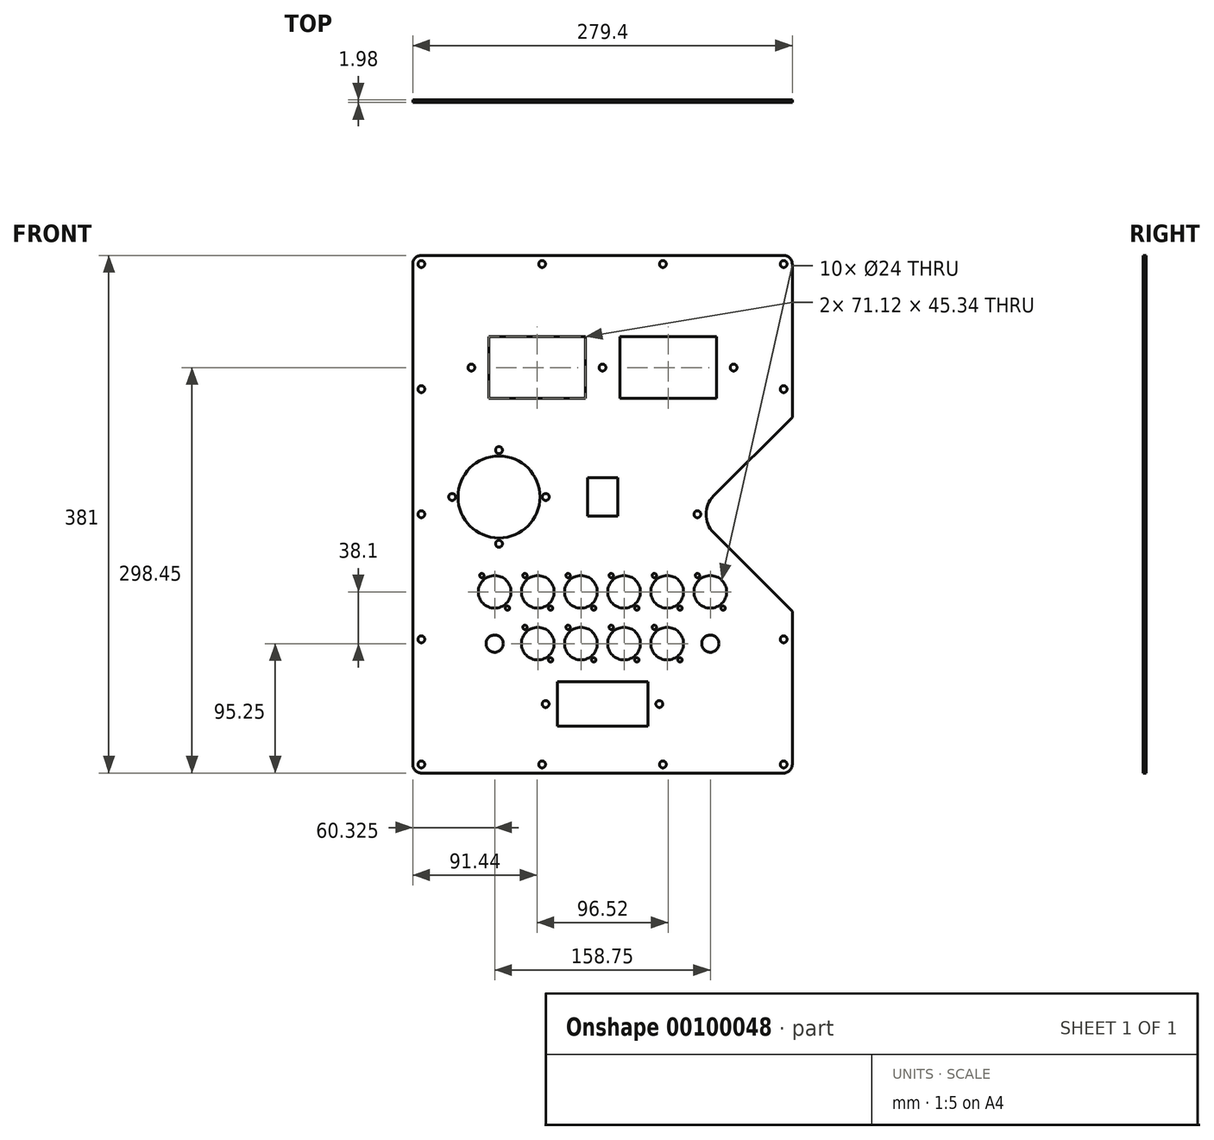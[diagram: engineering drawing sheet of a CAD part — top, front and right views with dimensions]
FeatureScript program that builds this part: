
annotation { "Feature Type Name" : "Feature", "Feature Type Description" : "" }
export const myFeature = defineFeature(function(context is Context, id is Id, definition is map)
    precondition{}
    {
        {
            var Q0;
            Q0=qCreatedBy(makeId("Front.planeOp"),FACE);
            var sketch = newSketch(context, id + "F0", { "sketchPlane" : qUnion([Q0])});
            skLineSegment(sketch, "E0.bottom", {"start": v(-139.7, 190.5) * mm, "end": v(139.7, 190.5) * mm});
            skLineSegment(sketch, "E0.top", {"start": v(-139.7, -190.5) * mm, "end": v(139.7, -190.5) * mm});
            skLineSegment(sketch, "E0.left", {"start": v(-139.7, 190.5) * mm, "end": v(-139.7, -190.5) * mm});
            skLineSegment(sketch, "E0.right", {"start": v(139.7, 190.5) * mm, "end": v(139.7, -190.5) * mm});
            skLineSegment(sketch, "E1", {"start": v(-139.7, 190.5) * mm, "end": v(139.7, -190.5) * mm, "construction": true});
            skLineSegment(sketch, "E2", {"start": v(139.7, 190.5) * mm, "end": v(-139.7, -190.5) * mm, "construction": true});
            skLineSegment(sketch, "E3", {"start": v(0, 190.5) * mm, "end": v(0, -190.5) * mm, "construction": true});
            skSolve(sketch);
        }
        {
            var Q0;
            Q0 = qSketchRegion(id + "F0", true);
            extrude(context, id + "F1", {"entities" : qUnion([Q0]), "depth" : 1.98 * mm});
        }
        {
            var Q0;
            Q0=makeQuery(id+"F1.opExtrude","CAP_FACE",FACE,{"disambiguationData":[OSD([sQuery(id+"F0.wireOp",EDGE,"E0.bottom"),sQuery(id+"F0.wireOp",EDGE,"E0.top"),sQuery(id+"F0.wireOp",EDGE,"E0.left"),sQuery(id+"F0.wireOp",EDGE,"E0.right")])],"isStart":false});
            var sketch = newSketch(context, id + "F2", { "sketchPlane" : qUnion([Q0])});
            skLineSegment(sketch, "E4.bottom", {"start": v(127, 177.8) * mm, "end": v(-127, 177.8) * mm});
            skLineSegment(sketch, "E4.top", {"start": v(127, -177.8) * mm, "end": v(-127, -177.8) * mm});
            skLineSegment(sketch, "E4.left", {"start": v(127, 177.8) * mm, "end": v(127, 76.65) * mm});
            skLineSegment(sketch, "E4.right", {"start": v(-127, 177.8) * mm, "end": v(-127, -177.8) * mm});
            skPoint(sketch, "E4.middle", {"position": v(0, 0) * mm});
            skArc(sketch, "E5", {"start": v(72.8, 22.45) * mm, "mid": v(63.5, 0) * mm, "end": v(72.8, -22.45) * mm});
            skLineSegment(sketch, "E6", {"start": v(72.8, 22.45) * mm, "end": v(127, 76.65) * mm});
            skLineSegment(sketch, "E7", {"start": v(72.8, -22.45) * mm, "end": v(127, -76.65) * mm});
            skLineSegment(sketch, "E8.trimOffspring", {"start": v(127, -76.65) * mm, "end": v(127, -177.8) * mm});
            skSolve(sketch);
        }
        {
            var Q0;
            Q0=makeQuery(id+"F1.opExtrude","CAP_FACE",FACE,{"disambiguationData":[OSD([sQuery(id+"F0.wireOp",EDGE,"E0.bottom"),sQuery(id+"F0.wireOp",EDGE,"E0.top"),sQuery(id+"F0.wireOp",EDGE,"E0.left"),sQuery(id+"F0.wireOp",EDGE,"E0.right")])],"isStart":false});
            var sketch = newSketch(context, id + "F3", { "sketchPlane" : qUnion([Q0])});
            skCircle(sketch, "E9", {"center": v(-76.2, 12.7) * mm, "radius": 30.16 * mm});
            skCircle(sketch, "E10", {"center": v(-76.2, 47.16) * mm, "radius": 2.54 * mm});
            skCircle(sketch, "E11", {"center": v(-41.74, 12.7) * mm, "radius": 2.54 * mm});
            skCircle(sketch, "E12", {"center": v(-76.2, -21.76) * mm, "radius": 2.54 * mm});
            skCircle(sketch, "E13", {"center": v(-110.66, 12.7) * mm, "radius": 2.54 * mm});
            skCircle(sketch, "E14", {"center": v(-76.2, 12.7) * mm, "radius": 34.46 * mm, "construction": true});
            skSolve(sketch);
        }
        {
            var Q0;
            Q0=makeQuery(id+"F1.opExtrude","CAP_FACE",FACE,{"disambiguationData":[OSD([sQuery(id+"F0.wireOp",EDGE,"E0.bottom"),sQuery(id+"F0.wireOp",EDGE,"E0.top"),sQuery(id+"F0.wireOp",EDGE,"E0.left"),sQuery(id+"F0.wireOp",EDGE,"E0.right")])],"isStart":false});
            var sketch = newSketch(context, id + "F4", { "sketchPlane" : qUnion([Q0])});
            skLineSegment(sketch, "E15.bottom", {"start": v(-11.11, 26.76) * mm, "end": v(11.11, 26.76) * mm});
            skLineSegment(sketch, "E15.top", {"start": v(-11.11, -1.36) * mm, "end": v(11.11, -1.36) * mm});
            skLineSegment(sketch, "E15.left", {"start": v(-11.11, 26.76) * mm, "end": v(-11.11, -1.36) * mm});
            skLineSegment(sketch, "E15.right", {"start": v(11.11, 26.76) * mm, "end": v(11.11, -1.36) * mm});
            skLineSegment(sketch, "E16", {"start": v(0, -1.36) * mm, "end": v(0, 0) * mm, "construction": true});
            skCircle(sketch, "E17.0", {"center": v(-76.2, 12.7) * mm, "radius": 34.46 * mm, "construction": true});
            skLineSegment(sketch, "E18", {"start": v(-76.2, 12.7) * mm, "end": v(-11.11, 12.7) * mm, "construction": true});
            skSolve(sketch);
        }
        {
            var Q0;
            Q0=makeQuery(id+"F1.opExtrude","CAP_FACE",FACE,{"disambiguationData":[OSD([sQuery(id+"F0.wireOp",EDGE,"E0.bottom"),sQuery(id+"F0.wireOp",EDGE,"E0.top"),sQuery(id+"F0.wireOp",EDGE,"E0.left"),sQuery(id+"F0.wireOp",EDGE,"E0.right")])],"isStart":false});
            var sketch = newSketch(context, id + "F5", { "sketchPlane" : qUnion([Q0])});
            skLineSegment(sketch, "E19.bottom", {"start": v(-83.82, 85.28) * mm, "end": v(-12.7, 85.28) * mm});
            skLineSegment(sketch, "E19.top", {"start": v(-83.82, 130.62) * mm, "end": v(-12.7, 130.62) * mm});
            skLineSegment(sketch, "E19.left", {"start": v(-83.82, 85.28) * mm, "end": v(-83.82, 130.62) * mm});
            skLineSegment(sketch, "E19.right", {"start": v(-12.7, 85.28) * mm, "end": v(-12.7, 130.62) * mm});
            skLineSegment(sketch, "E20.bottom", {"start": v(12.7, 85.28) * mm, "end": v(83.82, 85.28) * mm});
            skLineSegment(sketch, "E20.top", {"start": v(12.7, 130.62) * mm, "end": v(83.82, 130.62) * mm});
            skLineSegment(sketch, "E20.left", {"start": v(12.7, 85.28) * mm, "end": v(12.7, 130.62) * mm});
            skLineSegment(sketch, "E20.right", {"start": v(83.82, 85.28) * mm, "end": v(83.82, 130.62) * mm});
            skLineSegment(sketch, "E21", {"start": v(-83.82, 107.95) * mm, "end": v(-96.52, 107.95) * mm, "construction": true});
            skLineSegment(sketch, "E22", {"start": v(83.82, 107.95) * mm, "end": v(96.52, 107.95) * mm, "construction": true});
            skCircle(sketch, "E23", {"center": v(-96.52, 107.95) * mm, "radius": 2.54 * mm});
            skCircle(sketch, "E24", {"center": v(96.52, 107.95) * mm, "radius": 2.54 * mm});
            skLineSegment(sketch, "E25", {"start": v(-12.7, 107.95) * mm, "end": v(0, 107.95) * mm, "construction": true});
            skPoint(sketch, "E25.endSnap0", {"position": v(-12.7, 107.95) * mm});
            skLineSegment(sketch, "E26", {"start": v(12.7, 107.95) * mm, "end": v(0, 107.95) * mm, "construction": true});
            skCircle(sketch, "E27", {"center": v(0, 107.95) * mm, "radius": 2.54 * mm});
            skLineSegment(sketch, "E28", {"start": v(0, 107.95) * mm, "end": v(0, 0) * mm, "construction": true});
            skSolve(sketch);
        }
        {
            var Q0;
            Q0=makeQuery(id+"F1.opExtrude","CAP_FACE",FACE,{"disambiguationData":[OSD([sQuery(id+"F0.wireOp",EDGE,"E0.bottom"),sQuery(id+"F0.wireOp",EDGE,"E0.top"),sQuery(id+"F0.wireOp",EDGE,"E0.left"),sQuery(id+"F0.wireOp",EDGE,"E0.right"),sQuery(id+"F0.wireOp",EDGE,"h9IRMIpb-LSlu-fdTu-ycnf-mhpyygmtLJdv"),sQuery(id+"F0.wireOp",EDGE,"yYoEWnjZ-7jQh-CGfM-oPbc-j7pyWlvO7h1l"),sQuery(id+"F0.wireOp",EDGE,"NovJv7q1-vMpo-y6lM-6HwO-RKcohdMXKd2X"),sQuery(id+"F0.wireOp",EDGE,"Jd78Q13S-E8d5-oNmg-n0Bc-iBzX8L0d9LYk"),sQuery(id+"F0.wireOp",EDGE,"d569440b-4b0a-41ca-b9de-1d57797d9db2.0.1.0"),sQuery(id+"F0.wireOp",EDGE,"d569440b-4b0a-41ca-b9de-1d57797d9db2.0.1.1"),sQuery(id+"F0.wireOp",EDGE,"d569440b-4b0a-41ca-b9de-1d57797d9db2.0.1.2"),sQuery(id+"F0.wireOp",EDGE,"d569440b-4b0a-41ca-b9de-1d57797d9db2.0.1.3"),sQuery(id+"F0.wireOp",EDGE,"590198d3-f6c1-4934-8355-473c2aef56420.MirrorCS"),sQuery(id+"F0.wireOp",EDGE,"fb5975e0-c9aa-4f66-85a4-b5ec14ec1ced0.MirrorCS"),sQuery(id+"F0.wireOp",EDGE,"d673b164-0bbc-45ec-aa36-e85b659530970.MirrorCS"),sQuery(id+"F0.wireOp",EDGE,"a6f88071-2a8c-472b-9538-4447b179ac7b0.MirrorCS"),sQuery(id+"F0.wireOp",EDGE,"384c53e7-d2bd-4482-b8c2-024507e4105a0.MirrorCS"),sQuery(id+"F0.wireOp",EDGE,"c5e2c4c2-971b-4f43-83ae-2127a011e6c90.MirrorCS"),sQuery(id+"F0.wireOp",EDGE,"ec55bebb-8ae0-4cb5-937d-f917f98a93640.MirrorCS"),sQuery(id+"F0.wireOp",EDGE,"7c94f603-0cc5-4a8e-8c4c-9db3a374b4de0.MirrorCS")])],"isStart":false});
            var sketch = newSketch(context, id + "F6", { "sketchPlane" : qUnion([Q0])});
            skCircle(sketch, "E29", {"center": v(-79.37, -57.15) * mm, "radius": 12 * mm});
            skCircle(sketch, "E30", {"center": v(-88.84, -45.15) * mm, "radius": 1.59 * mm});
            skCircle(sketch, "E31", {"center": v(-69.91, -69.15) * mm, "radius": 1.59 * mm});
            skLineSegment(sketch, "E32", {"start": v(-79.37, -57.15) * mm, "end": v(-88.84, -45.15) * mm, "construction": true});
            skLineSegment(sketch, "E33", {"start": v(-79.37, -57.15) * mm, "end": v(-69.91, -69.15) * mm, "construction": true});
            skCircle(sketch, "E34.1.0.0", {"center": v(-47.62, -57.15) * mm, "radius": 12 * mm});
            skCircle(sketch, "E34.1.0.1", {"center": v(-57.09, -45.15) * mm, "radius": 1.59 * mm});
            skCircle(sketch, "E34.1.0.2", {"center": v(-38.16, -69.15) * mm, "radius": 1.59 * mm});
            skLineSegment(sketch, "E34.1.0.3", {"start": v(-47.62, -57.15) * mm, "end": v(-38.16, -69.15) * mm, "construction": true});
            skLineSegment(sketch, "E34.1.0.4", {"start": v(-47.62, -57.15) * mm, "end": v(-57.09, -45.15) * mm, "construction": true});
            skCircle(sketch, "E34.2.0.0", {"center": v(-15.87, -57.15) * mm, "radius": 12 * mm});
            skCircle(sketch, "E34.2.0.1", {"center": v(-25.34, -45.15) * mm, "radius": 1.59 * mm});
            skCircle(sketch, "E34.2.0.2", {"center": v(-6.41, -69.15) * mm, "radius": 1.59 * mm});
            skLineSegment(sketch, "E34.2.0.3", {"start": v(-15.87, -57.15) * mm, "end": v(-6.41, -69.15) * mm, "construction": true});
            skLineSegment(sketch, "E34.2.0.4", {"start": v(-15.87, -57.15) * mm, "end": v(-25.34, -45.15) * mm, "construction": true});
            skCircle(sketch, "E34.3.0.0", {"center": v(15.88, -57.15) * mm, "radius": 12 * mm});
            skCircle(sketch, "E34.3.0.1", {"center": v(6.41, -45.15) * mm, "radius": 1.59 * mm});
            skCircle(sketch, "E34.3.0.2", {"center": v(25.34, -69.15) * mm, "radius": 1.59 * mm});
            skLineSegment(sketch, "E34.3.0.3", {"start": v(15.88, -57.15) * mm, "end": v(25.34, -69.15) * mm, "construction": true});
            skLineSegment(sketch, "E34.3.0.4", {"start": v(15.88, -57.15) * mm, "end": v(6.41, -45.15) * mm, "construction": true});
            skCircle(sketch, "E34.4.0.0", {"center": v(47.62, -57.15) * mm, "radius": 12 * mm});
            skCircle(sketch, "E34.4.0.1", {"center": v(38.16, -45.15) * mm, "radius": 1.59 * mm});
            skCircle(sketch, "E34.4.0.2", {"center": v(57.09, -69.15) * mm, "radius": 1.59 * mm});
            skLineSegment(sketch, "E34.4.0.3", {"start": v(47.63, -57.15) * mm, "end": v(57.09, -69.15) * mm, "construction": true});
            skLineSegment(sketch, "E34.4.0.4", {"start": v(47.63, -57.15) * mm, "end": v(38.16, -45.15) * mm, "construction": true});
            skCircle(sketch, "E34.5.0.0", {"center": v(79.37, -57.15) * mm, "radius": 12 * mm});
            skCircle(sketch, "E34.5.0.1", {"center": v(69.91, -45.15) * mm, "radius": 1.59 * mm});
            skCircle(sketch, "E34.5.0.2", {"center": v(88.84, -69.15) * mm, "radius": 1.59 * mm});
            skLineSegment(sketch, "E34.5.0.3", {"start": v(79.38, -57.15) * mm, "end": v(88.84, -69.15) * mm, "construction": true});
            skLineSegment(sketch, "E34.5.0.4", {"start": v(79.38, -57.15) * mm, "end": v(69.91, -45.15) * mm, "construction": true});
            skLineSegment(sketch, "E34.direction1", {"start": v(-79.37, -57.15) * mm, "end": v(-47.62, -57.15) * mm, "construction": true});
            skLineSegment(sketch, "E35", {"start": v(-15.87, -57.15) * mm, "end": v(15.88, -57.15) * mm, "construction": true});
            skLineSegment(sketch, "E36", {"start": v(0, 0) * mm, "end": v(0, -57.15) * mm, "construction": true});
            skSolve(sketch);
        }
        {
            var Q0;
            Q0=makeQuery(id+"F1.opExtrude","CAP_FACE",FACE,{"disambiguationData":[OSD([sQuery(id+"F0.wireOp",EDGE,"E0.bottom"),sQuery(id+"F0.wireOp",EDGE,"E0.top"),sQuery(id+"F0.wireOp",EDGE,"E0.left"),sQuery(id+"F0.wireOp",EDGE,"E0.right")])],"isStart":false});
            var sketch = newSketch(context, id + "F7", { "sketchPlane" : qUnion([Q0])});
            skCircle(sketch, "E37", {"center": v(-47.62, -95.25) * mm, "radius": 12 * mm});
            skCircle(sketch, "E38", {"center": v(-57.09, -83.25) * mm, "radius": 1.59 * mm});
            skCircle(sketch, "E39", {"center": v(-38.16, -107.25) * mm, "radius": 1.59 * mm});
            skLineSegment(sketch, "E40", {"start": v(-57.09, -83.25) * mm, "end": v(-47.62, -95.25) * mm, "construction": true});
            skLineSegment(sketch, "E41", {"start": v(-38.16, -107.25) * mm, "end": v(-47.62, -95.25) * mm, "construction": true});
            skCircle(sketch, "E42.1.0.0", {"center": v(-15.87, -95.25) * mm, "radius": 12 * mm});
            skLineSegment(sketch, "E42.1.0.1", {"start": v(-6.41, -107.25) * mm, "end": v(-15.87, -95.25) * mm, "construction": true});
            skLineSegment(sketch, "E42.1.0.2", {"start": v(-25.34, -83.25) * mm, "end": v(-15.87, -95.25) * mm, "construction": true});
            skCircle(sketch, "E42.1.0.3", {"center": v(-25.34, -83.25) * mm, "radius": 1.59 * mm});
            skCircle(sketch, "E42.1.0.4", {"center": v(-6.41, -107.25) * mm, "radius": 1.59 * mm});
            skCircle(sketch, "E42.2.0.0", {"center": v(15.88, -95.25) * mm, "radius": 12 * mm});
            skLineSegment(sketch, "E42.2.0.1", {"start": v(25.34, -107.25) * mm, "end": v(15.88, -95.25) * mm, "construction": true});
            skLineSegment(sketch, "E42.2.0.2", {"start": v(6.41, -83.25) * mm, "end": v(15.88, -95.25) * mm, "construction": true});
            skCircle(sketch, "E42.2.0.3", {"center": v(6.41, -83.25) * mm, "radius": 1.59 * mm});
            skCircle(sketch, "E42.2.0.4", {"center": v(25.34, -107.25) * mm, "radius": 1.59 * mm});
            skCircle(sketch, "E42.3.0.0", {"center": v(47.63, -95.25) * mm, "radius": 12 * mm});
            skLineSegment(sketch, "E42.3.0.1", {"start": v(57.09, -107.25) * mm, "end": v(47.63, -95.25) * mm, "construction": true});
            skLineSegment(sketch, "E42.3.0.2", {"start": v(38.16, -83.25) * mm, "end": v(47.63, -95.25) * mm, "construction": true});
            skCircle(sketch, "E42.3.0.3", {"center": v(38.16, -83.25) * mm, "radius": 1.59 * mm});
            skCircle(sketch, "E42.3.0.4", {"center": v(57.09, -107.25) * mm, "radius": 1.59 * mm});
            skLineSegment(sketch, "E42.direction1", {"start": v(-47.62, -95.25) * mm, "end": v(-15.87, -95.25) * mm, "construction": true});
            skLineSegment(sketch, "E43", {"start": v(-47.62, -95.25) * mm, "end": v(-79.37, -95.25) * mm, "construction": true});
            skLineSegment(sketch, "E44", {"start": v(47.63, -95.25) * mm, "end": v(79.38, -95.25) * mm, "construction": true});
            skCircle(sketch, "E45", {"center": v(-79.37, -95.25) * mm, "radius": 6.35 * mm});
            skCircle(sketch, "E46", {"center": v(79.38, -95.25) * mm, "radius": 6.35 * mm});
            skSolve(sketch);
        }
        {
            var Q0;
            Q0=makeQuery(id+"F1.opExtrude","CAP_FACE",FACE,{"disambiguationData":[OSD([sQuery(id+"F0.wireOp",EDGE,"E0.bottom"),sQuery(id+"F0.wireOp",EDGE,"E0.top"),sQuery(id+"F0.wireOp",EDGE,"E0.left"),sQuery(id+"F0.wireOp",EDGE,"E0.right")])],"isStart":false});
            var sketch = newSketch(context, id + "F8", { "sketchPlane" : qUnion([Q0])});
            skLineSegment(sketch, "E47.bottom", {"start": v(33.34, -155.96) * mm, "end": v(33.34, -123.44) * mm});
            skLineSegment(sketch, "E47.top", {"start": v(-33.34, -155.96) * mm, "end": v(-33.34, -123.44) * mm});
            skLineSegment(sketch, "E47.left", {"start": v(33.34, -155.96) * mm, "end": v(-33.34, -155.96) * mm});
            skLineSegment(sketch, "E47.right", {"start": v(33.34, -123.44) * mm, "end": v(-33.34, -123.44) * mm});
            skCircle(sketch, "E48", {"center": v(-41.85, -139.7) * mm, "radius": 2.54 * mm});
            skCircle(sketch, "E49", {"center": v(41.85, -139.7) * mm, "radius": 2.54 * mm});
            skLineSegment(sketch, "E50", {"start": v(-41.85, -139.7) * mm, "end": v(-33.34, -139.7) * mm, "construction": true});
            skLineSegment(sketch, "E51", {"start": v(-33.34, -139.7) * mm, "end": v(33.34, -139.7) * mm, "construction": true});
            skLineSegment(sketch, "E52", {"start": v(33.34, -139.7) * mm, "end": v(41.85, -139.7) * mm, "construction": true});
            skLineSegment(sketch, "E53", {"start": v(0, -139.7) * mm, "end": v(0, 0) * mm, "construction": true});
            skSolve(sketch);
        }
        {
            var Q0;
            Q0 = qSketchRegion(id + "F6", true);
            var Q1;
            Q1 = qSketchRegion(id + "F3", true);
            var Q2;
            Q2 = qSketchRegion(id + "F5", true);
            var Q3;
            Q3 = qSketchRegion(id + "F7", true);
            var Q4;
            Q4 = qSketchRegion(id + "F4", true);
            var Q5;
            Q5 = qSketchRegion(id + "F8", true);
            extrude(context, id + "F9", {"entities" : qUnion([Q0, Q1, Q2, Q3, Q4, Q5]), "operationType" : NewBodyOperationType.REMOVE, "oppositeDirection" : true, "depth" : 25.4 * mm});
        }
        {
            var Q0;
            Q0=makeQuery(id+"F1.opExtrude","CAP_FACE",FACE,{"disambiguationData":[OSD([sQuery(id+"F0.wireOp",EDGE,"E0.bottom"),sQuery(id+"F0.wireOp",EDGE,"E0.top"),sQuery(id+"F0.wireOp",EDGE,"E0.left"),sQuery(id+"F0.wireOp",EDGE,"E0.right")])],"isStart":false});
            var sketch = newSketch(context, id + "F10", { "sketchPlane" : qUnion([Q0])});
            skLineSegment(sketch, "E54.0", {"start": v(81.78, 13.47) * mm, "end": v(139.7, 71.4) * mm});
            skArc(sketch, "E54.1", {"start": v(81.78, 13.47) * mm, "mid": v(76.2, 0) * mm, "end": v(81.78, -13.47) * mm});
            skLineSegment(sketch, "E54.2", {"start": v(81.78, -13.47) * mm, "end": v(139.7, -71.4) * mm});
            skLineSegment(sketch, "E55.0", {"start": v(139.7, 71.4) * mm, "end": v(139.7, -71.4) * mm});
            skPoint(sketch, "E56.orphan", {"position": v(139.7, 190.5) * mm});
            skPoint(sketch, "E57.orphan", {"position": v(139.7, -190.5) * mm});
            skSolve(sketch);
        }
        {
            var Q0;
            Q0 = qSketchRegion(id + "F10", true);
            extrude(context, id + "F11", {"entities" : qUnion([Q0]), "operationType" : NewBodyOperationType.REMOVE, "oppositeDirection" : true, "depth" : 25.4 * mm});
        }
        {
            var Q0;
            Q0=makeQuery(id+"F1.opExtrude","CAP_FACE",FACE,{"disambiguationData":[OSD([sQuery(id+"F0.wireOp",EDGE,"E0.bottom"),sQuery(id+"F0.wireOp",EDGE,"E0.top"),sQuery(id+"F0.wireOp",EDGE,"E0.left"),sQuery(id+"F0.wireOp",EDGE,"E0.right")])],"isStart":false});
            var sketch = newSketch(context, id + "F12", { "sketchPlane" : qUnion([Q0])});
            skCircle(sketch, "E58", {"center": v(-133.35, 184.15) * mm, "radius": 2.54 * mm});
            skCircle(sketch, "E59", {"center": v(133.35, 184.15) * mm, "radius": 2.54 * mm});
            skCircle(sketch, "E60", {"center": v(133.35, 92.08) * mm, "radius": 2.54 * mm});
            skCircle(sketch, "E61", {"center": v(133.35, -92.08) * mm, "radius": 2.54 * mm});
            skCircle(sketch, "E62", {"center": v(133.35, -184.15) * mm, "radius": 2.54 * mm});
            skCircle(sketch, "E63", {"center": v(-133.35, -184.15) * mm, "radius": 2.54 * mm});
            skCircle(sketch, "E64", {"center": v(-133.35, -92.08) * mm, "radius": 2.54 * mm});
            skCircle(sketch, "E65", {"center": v(-133.35, 92.07) * mm, "radius": 2.54 * mm});
            skCircle(sketch, "E66", {"center": v(-133.35, 0) * mm, "radius": 2.54 * mm});
            skCircle(sketch, "E67", {"center": v(-44.45, 184.15) * mm, "radius": 2.54 * mm});
            skCircle(sketch, "E68", {"center": v(-44.45, -184.15) * mm, "radius": 2.54 * mm});
            skLineSegment(sketch, "E69", {"start": v(-133.35, 184.15) * mm, "end": v(-133.35, 92.07) * mm, "construction": true});
            skLineSegment(sketch, "E70", {"start": v(-133.35, 0) * mm, "end": v(-133.35, -92.08) * mm, "construction": true});
            skLineSegment(sketch, "E71", {"start": v(-133.35, 92.07) * mm, "end": v(-133.35, 0) * mm, "construction": true});
            skLineSegment(sketch, "E72", {"start": v(-133.35, -92.08) * mm, "end": v(-133.35, -184.15) * mm, "construction": true});
            skCircle(sketch, "E73", {"center": v(44.45, 184.15) * mm, "radius": 2.54 * mm});
            skCircle(sketch, "E74", {"center": v(44.45, -184.15) * mm, "radius": 2.54 * mm});
            skLineSegment(sketch, "E75", {"start": v(-133.35, 184.15) * mm, "end": v(-44.45, 184.15) * mm, "construction": true});
            skLineSegment(sketch, "E76", {"start": v(-44.45, 184.15) * mm, "end": v(44.45, 184.15) * mm, "construction": true});
            skLineSegment(sketch, "E77", {"start": v(44.45, 184.15) * mm, "end": v(133.35, 184.15) * mm, "construction": true});
            skCircle(sketch, "E78", {"center": v(69.85, 0) * mm, "radius": 2.54 * mm});
            skSolve(sketch);
        }
        {
            var Q0;
            Q0 = qSketchRegion(id + "F12", true);
            extrude(context, id + "F13", {"entities" : qUnion([Q0]), "operationType" : NewBodyOperationType.REMOVE, "oppositeDirection" : true, "depth" : 25.4 * mm});
        }
        {
            var Q0;
            Q0=makeQuery(id+"F1.opExtrude","SWEPT_EDGE",EDGE,{"disambiguationData":[OSD([sQuery(id+"F0.wireOp",EDGE,"E0.bottom"),sQuery(id+"F0.wireOp",EDGE,"E0.left")])]});
            var Q1;
            Q1=makeQuery(id+"F1.opExtrude","SWEPT_EDGE",EDGE,{"disambiguationData":[OSD([sQuery(id+"F0.wireOp",EDGE,"E0.bottom"),sQuery(id+"F0.wireOp",EDGE,"E0.right")])]});
            var Q2;
            Q2=makeQuery(id+"F11.boolean.opBoolean","COPY",EDGE,{"derivedFrom":makeQuery(id+"F11.opExtrude","SWEPT_EDGE",EDGE,{"disambiguationData":[OSD([sQuery(id+"F0.wireOp",EDGE,"E0.right"),sQuery(id+"F10.wireOp",EDGE,"E54.0"),sQuery(id+"F10.wireOp",EDGE,"E55.0")])]})});
            var Q3;
            Q3=makeQuery(id+"F11.boolean.opBoolean","COPY",EDGE,{"derivedFrom":makeQuery(id+"F11.opExtrude","SWEPT_EDGE",EDGE,{"disambiguationData":[OSD([sQuery(id+"F0.wireOp",EDGE,"E0.right"),sQuery(id+"F10.wireOp",EDGE,"E54.2"),sQuery(id+"F10.wireOp",EDGE,"E55.0")])]})});
            var Q4;
            Q4=makeQuery(id+"F1.opExtrude","SWEPT_EDGE",EDGE,{"disambiguationData":[OSD([sQuery(id+"F0.wireOp",EDGE,"E0.top"),sQuery(id+"F0.wireOp",EDGE,"E0.right")])]});
            var Q5;
            Q5=makeQuery(id+"F1.opExtrude","SWEPT_EDGE",EDGE,{"disambiguationData":[OSD([sQuery(id+"F0.wireOp",EDGE,"E0.top"),sQuery(id+"F0.wireOp",EDGE,"E0.left")])]});
            fillet(context, id + "F14", {"entities" : qUnion([Q0, Q1, Q2, Q3, Q4, Q5]), "radius" : 6.35 * mm, "tangentPropagation" : true, "allowEdgeOverflow" : false});
        }
    });
